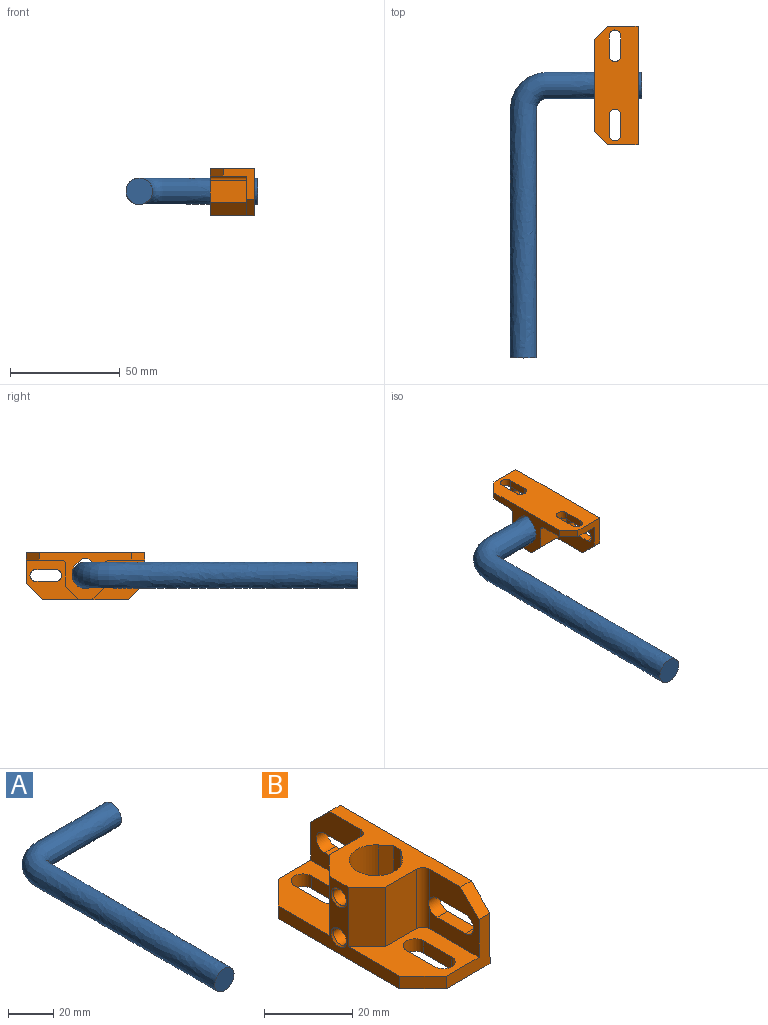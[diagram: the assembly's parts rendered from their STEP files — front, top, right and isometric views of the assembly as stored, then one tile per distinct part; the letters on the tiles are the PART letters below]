
ASSEMBLY  parts=2 mates=1
PART A: 3 faces, bbox 60x130x12 mm
  f0: plane 12.02x12.02mm, normal (1,0,0), area 113mm2, adj f2
  f1: plane 12.02x12.02mm, normal (0,-1,0), area 113mm2, adj f2
  f2: bspline ~130.01x60.01mm, area 6532mm2, adj f0,f1
PART B: 46 faces, bbox 21.5x54x20 mm
  f0: plane 42x21.5mm, normal (0,0,1), area 317.9mm2, adj f2,f3,f4,f12,f15,f19,f22,f23
  f1: plane 24x18mm, normal (0,0,1), area 241.5mm2, adj f8,f9,f10,f12,f13,f14,f17,f25
  f2: cylinder r=6.05mm len=20mm, axis (0,0,-1), area 551mm2, adj f0,f3,f19,f21,f32,f35
  f3: plane 20x2.71mm, normal (-0.77,-0.64,0), area 70.2mm2, adj f0,f2,f4,f21
  f4: plane 20x2.28mm, normal (-1,0,0), area 45.6mm2, adj f0,f3,f19,f21
  f5: plane 9x3.5mm, normal (-1,0,0), area 31.5mm2, adj f6,f16,f20,f21
  f6: cylinder r=2.7mm len=5.4mm, axis (0,0,-1), area 29.7mm2, adj f5,f7,f20,f21
  f7: plane 9x3.5mm, normal (1,0,0), area 31.5mm2, adj f6,f16,f20,f21
  f8: plane 9x3.5mm, normal (1,0,0), area 31.5mm2, adj f1,f9,f17,f21
  f9: cylinder r=2.7mm len=5.4mm, axis (0,0,-1), area 29.7mm2, adj f1,f8,f10,f21
  f10: plane 9x3.5mm, normal (-1,0,0), area 31.5mm2, adj f1,f9,f17,f21
  f11: plane 7.5x7.5mm, normal (-0.71,0.71,0), area 37.1mm2, adj f12,f18,f20,f21
  f12: plane 39x20mm, normal (-1,0,0), area 196.2mm2, adj f0,f1,f11,f13,f20,f21,f24,f25
  f13: plane 7.5x7.5mm, normal (-0.71,-0.71,0), area 37.1mm2, adj f1,f12,f14,f21
  f14: plane 14x14mm, normal (0,-1,0), area 85.8mm2, adj f1,f13,f15,f21,f27,f36
  f15: plane 54x20mm, normal (1,0,0), area 901mm2, adj f0,f14,f18,f21,f36,f37,f38,f39
  f16: cylinder r=2.7mm len=5.4mm, axis (0,0,-1), area 29.7mm2, adj f5,f7,f20,f21
  f17: cylinder r=2.7mm len=5.4mm, axis (0,0,-1), area 29.7mm2, adj f1,f8,f10,f21
  f18: plane 14x14mm, normal (0,1,0), area 85.7mm2, adj f11,f15,f20,f21,f22,f37
  f19: plane 20x2.71mm, normal (-0.77,0.64,0), area 70.2mm2, adj f0,f2,f4,f21
  f20: plane 24x18mm, normal (0,0,1), area 241.5mm2, adj f5,f6,f7,f11,f12,f16,f18,f22
  f21: plane 54x21.5mm, normal (0,0,-1), area 842.9mm2, adj f2,f3,f4,f5,f6,f7,f8,f9
  f22: plane 16.5x16mm, normal (-1,0,0), area 174.8mm2, adj f0,f18,f20,f28,f37,f38,f39,f42
  f23: plane 16.5x10mm, normal (0,1,0), area 165mm2, adj f0,f20,f24,f28
  f24: plane 16.5x6mm, normal (-0.71,0.71,0), area 140mm2, adj f0,f12,f20,f23
  f25: plane 16.5x6mm, normal (-0.71,-0.71,0), area 140mm2, adj f0,f1,f12,f26
  f26: plane 16.5x10mm, normal (0,-1,0), area 165mm2, adj f0,f1,f25,f29
  f27: plane 16.5x16mm, normal (-1,0,0), area 174.8mm2, adj f0,f1,f14,f29,f36,f40,f41,f44
  f28: cylinder r=2mm len=16.5mm, axis (0,0,1), area 51.8mm2, adj f0,f20,f22,f23,f43
  f29: cylinder r=2mm len=16.5mm, axis (0,0,1), area 51.8mm2, adj f0,f1,f26,f27,f45
  f30: cylinder r=2.1mm len=4.96mm, axis (1,0,0), area 65.4mm2, adj f31,f32
  f31: cone r=2.5mm half-angle=45deg, axis (-1,0,0), area 8.2mm2, adj f12,f30
  f32: bspline ~5.35x4.94mm, area 10mm2, adj f2,f30
  f33: cylinder r=2.1mm len=4.96mm, axis (1,0,0), area 65.4mm2, adj f34,f35
  f34: cone r=2.5mm half-angle=45deg, axis (-1,0,0), area 8.2mm2, adj f12,f33
  f35: bspline ~5.35x4.94mm, area 10mm2, adj f2,f33
  f36: plane 6x6mm, normal (0,-0.71,0.71), area 29.7mm2, adj f0,f14,f15,f27
  f37: plane 6x6mm, normal (0,0.71,0.71), area 29.7mm2, adj f0,f15,f18,f22
  f38: plane 9x3.5mm, normal (0,0,-1), area 31.5mm2, adj f15,f22,f42,f43
  f39: plane 9x3.5mm, normal (0,0,1), area 31.5mm2, adj f15,f22,f42,f43
  f40: plane 9x3.5mm, normal (0,0,-1), area 31.5mm2, adj f15,f27,f44,f45
  f41: plane 9x3.5mm, normal (0,0,1), area 31.5mm2, adj f15,f27,f44,f45
  f42: cylinder r=2.7mm len=5.4mm, axis (1,0,0), area 29.7mm2, adj f15,f22,f38,f39
  f43: cylinder r=2.7mm len=5.4mm, axis (1,0,0), area 29.7mm2, adj f15,f22,f28,f38,f39
  f44: cylinder r=2.7mm len=5.4mm, axis (1,0,0), area 29.7mm2, adj f15,f27,f40,f41
  f45: cylinder r=2.7mm len=5.4mm, axis (1,0,0), area 29.7mm2, adj f15,f27,f29,f40,f41
PLACE A t=(-9.06,-46.67,13.16)mm
PLACE B rot(axis=(0,-1,0),90deg) t=(43.18,50.33,23.59)mm
MATE cylindrical B.f21 <-> A.f0  axis (1,0,0) through (43.18,77.33,13.16)mm
